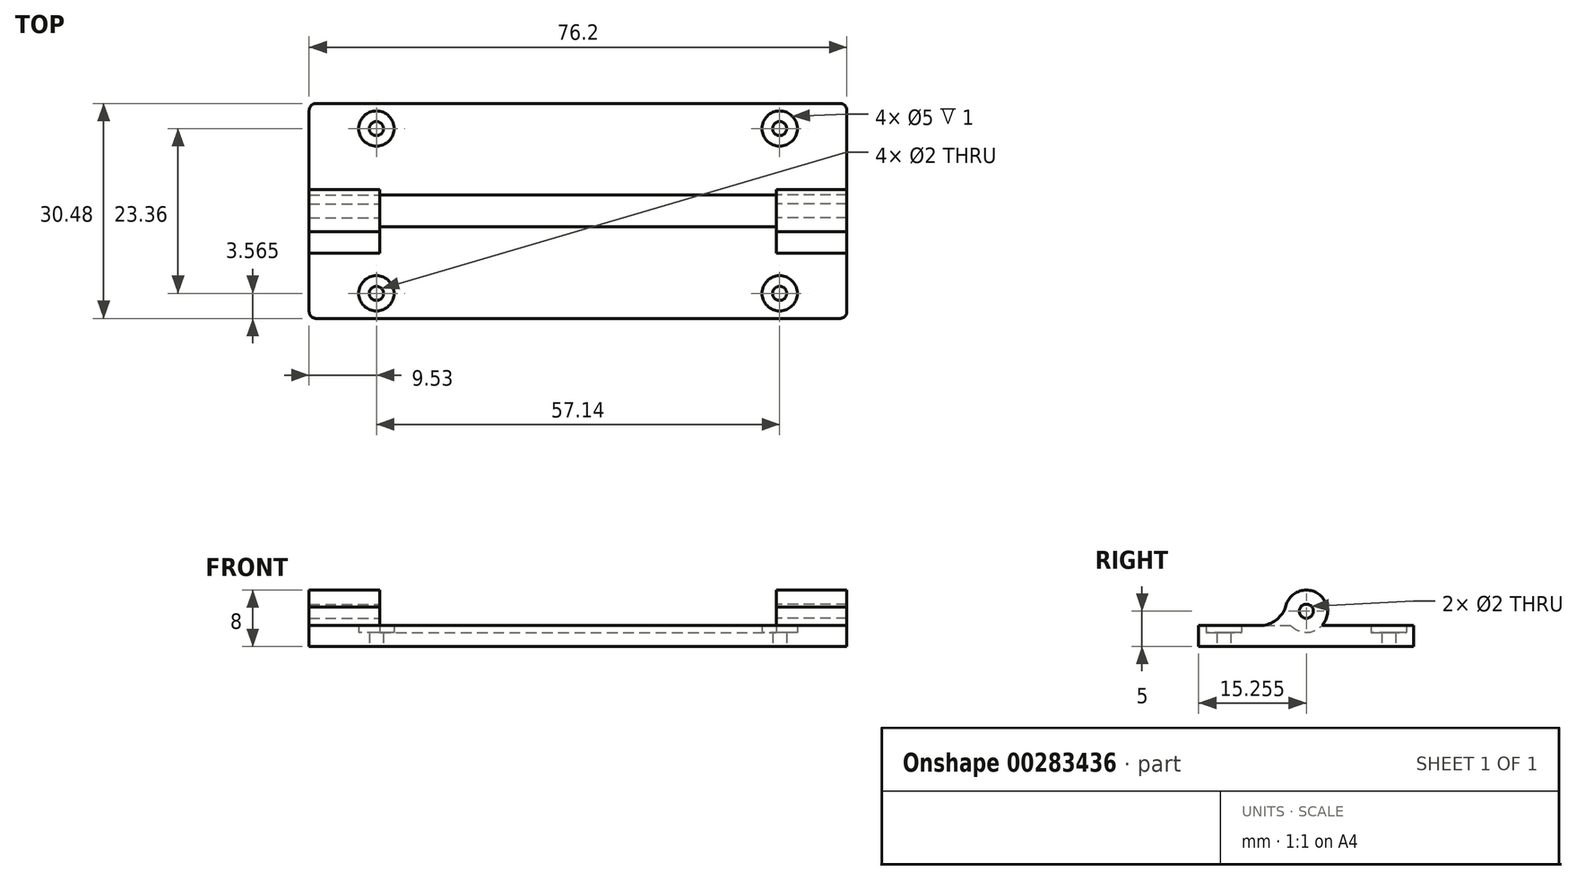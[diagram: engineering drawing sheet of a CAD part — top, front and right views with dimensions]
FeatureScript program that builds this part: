
annotation { "Feature Type Name" : "Feature", "Feature Type Description" : "" }
export const myFeature = defineFeature(function(context is Context, id is Id, definition is map)
    precondition{}
    {
        {
            var Q0;
            Q0=qCreatedBy(makeId("Top.planeOp"),FACE);
            var sketch = newSketch(context, id + "F0", { "sketchPlane" : qUnion([Q0])});
            skLineSegment(sketch, "E0.bottom", {"start": v(-38.1, -13.62) * mm, "end": v(38.1, -13.62) * mm});
            skLineSegment(sketch, "E0.top", {"start": v(-38.1, 16.86) * mm, "end": v(38.1, 16.86) * mm});
            skLineSegment(sketch, "E0.left", {"start": v(-38.1, -13.62) * mm, "end": v(-38.1, 16.86) * mm});
            skLineSegment(sketch, "E0.right", {"start": v(38.1, -13.62) * mm, "end": v(38.1, 16.86) * mm});
            skCircle(sketch, "E1", {"center": v(-28.57, -10.06) * mm, "radius": 1 * mm});
            skCircle(sketch, "E2", {"center": v(28.57, -10.06) * mm, "radius": 1 * mm});
            skCircle(sketch, "E3", {"center": v(28.57, 13.3) * mm, "radius": 1 * mm});
            skCircle(sketch, "E4", {"center": v(-28.57, 13.3) * mm, "radius": 1 * mm});
            skCircle(sketch, "E5", {"center": v(-28.57, 13.3) * mm, "radius": 2.5 * mm});
            skCircle(sketch, "E6", {"center": v(28.57, 13.3) * mm, "radius": 2.5 * mm});
            skCircle(sketch, "E7", {"center": v(28.57, -10.06) * mm, "radius": 2.5 * mm});
            skCircle(sketch, "E8", {"center": v(-28.57, -10.06) * mm, "radius": 2.5 * mm});
            skSolve(sketch);
        }
        {
            var Q0;
            Q0=qCreatedBy(makeId("Right.planeOp"),FACE);
            var sketch = newSketch(context, id + "F1", { "sketchPlane" : qUnion([Q0])});
            skLineSegment(sketch, "E9.bottom", {"start": v(-13.62, 0) * mm, "end": v(16.86, 0) * mm});
            skLineSegment(sketch, "E9.top", {"start": v(-13.62, 3) * mm, "end": v(16.86, 3) * mm});
            skLineSegment(sketch, "E9.left", {"start": v(-13.62, 0) * mm, "end": v(-13.62, 3) * mm});
            skLineSegment(sketch, "E9.right", {"start": v(16.86, 0) * mm, "end": v(16.86, 3) * mm});
            skCircle(sketch, "E10", {"center": v(1.63, 5) * mm, "radius": 3 * mm});
            skLineSegment(sketch, "E11", {"start": v(-4.37, 3) * mm, "end": v(-4.37, 5) * mm});
            skArc(sketch, "E12", {"start": v(-4.37, 3) * mm, "mid": v(-2.5, 3.87) * mm, "end": v(-1.31, 5.56) * mm});
            skLineSegment(sketch, "E13", {"start": v(1.63, 5) * mm, "end": v(1.63, 4) * mm});
            skArc(sketch, "E14.MirrorCS", {"start": v(7.63, 3) * mm, "mid": v(5.77, 3.87) * mm, "end": v(4.58, 5.56) * mm});
            skCircle(sketch, "E15", {"center": v(1.63, 5) * mm, "radius": 1 * mm});
            skSolve(sketch);
        }
        {
            var Q0;
            Q0=makeQuery(id+"F0.imprint","IMPRINT",FACE,{"disambiguationData":[TD([[makeQuery(id+"F0.imprint","IMPRINT",EDGE,{"derivedFrom":sQuery(id+"F0.wireOp",EDGE,"E0.bottom")}),1.0]])]});
            extrude(context, id + "F2", {"entities" : qUnion([Q0]), "depth" : 3 * mm, "offsetDistance" : 25 * mm});
        }
        {
            var Q0;
            Q0=makeQuery(id+"F0.imprint","IMPRINT",FACE,{"disambiguationData":[TD([[makeQuery(id+"F0.imprint","IMPRINT",EDGE,{"derivedFrom":sQuery(id+"F0.wireOp",EDGE,"E3")}),-1.0]])]});
            var Q1;
            Q1=makeQuery(id+"F0.imprint","IMPRINT",FACE,{"disambiguationData":[TD([[makeQuery(id+"F0.imprint","IMPRINT",EDGE,{"derivedFrom":sQuery(id+"F0.wireOp",EDGE,"E2")}),-1.0]])]});
            var Q2;
            Q2=makeQuery(id+"F0.imprint","IMPRINT",FACE,{"disambiguationData":[TD([[makeQuery(id+"F0.imprint","IMPRINT",EDGE,{"derivedFrom":sQuery(id+"F0.wireOp",EDGE,"E1")}),-1.0]])]});
            var Q3;
            Q3=makeQuery(id+"F0.imprint","IMPRINT",FACE,{"disambiguationData":[TD([[makeQuery(id+"F0.imprint","IMPRINT",EDGE,{"derivedFrom":sQuery(id+"F0.wireOp",EDGE,"E4")}),-1.0]])]});
            extrude(context, id + "F3", {"entities" : qUnion([Q0, Q1, Q2, Q3]), "operationType" : NewBodyOperationType.ADD, "depth" : 2 * mm, "offsetDistance" : 25 * mm});
        }
        {
            var Q0;
            {var subQ0=sQuery(id+"F1.wireOp",EDGE,"E14.MirrorCS");Q0=makeQuery(id+"F1.imprint","IMPRINT",FACE,{"disambiguationData":[TD([[makeQuery(id+"F1.imprint","IMPRINT",EDGE,{"derivedFrom":subQ0}),1.0]])]});}
            var Q1;
            {var subQ7=sQuery(id+"F1.wireOp",EDGE,"E15");var subQ8=makeQuery(id+"F1.imprint","IMPRINT",VERTEX,{"disambiguationData":[OD(0.0)],"derivedFrom":subQ7});Q1=makeQuery(id+"F1.imprint","IMPRINT",FACE,{"disambiguationData":[TD([[makeQuery(id+"F1.imprint","IMPRINT",EDGE,{"disambiguationData":[TD([[subQ8,-1.0]])],"derivedFrom":subQ7}),-1.0]])]});}
            var Q2;
            {var subQ3=sQuery(id+"F1.wireOp",EDGE,"E12");Q2=makeQuery(id+"F1.imprint","IMPRINT",FACE,{"disambiguationData":[TD([[makeQuery(id+"F1.imprint","IMPRINT",EDGE,{"derivedFrom":subQ3}),-1.0]])]});}
            extrude(context, id + "F4", {"entities" : qUnion([Q0, Q1, Q2]), "operationType" : NewBodyOperationType.ADD, "depth" : 38.1 * mm, "offsetDistance" : 25 * mm, "hasSecondDirection" : true, "secondDirectionOppositeDirection" : false, "secondDirectionDepth" : 28.1 * mm});
        }
        {
            var Q0;
            {var subQ0=sQuery(id+"F1.wireOp",EDGE,"E14.MirrorCS");Q0=makeQuery(id+"F1.imprint","IMPRINT",FACE,{"disambiguationData":[TD([[makeQuery(id+"F1.imprint","IMPRINT",EDGE,{"derivedFrom":subQ0}),1.0]])]});}
            var Q1;
            {var subQ7=sQuery(id+"F1.wireOp",EDGE,"E15");var subQ8=makeQuery(id+"F1.imprint","IMPRINT",VERTEX,{"disambiguationData":[OD(0.0)],"derivedFrom":subQ7});Q1=makeQuery(id+"F1.imprint","IMPRINT",FACE,{"disambiguationData":[TD([[makeQuery(id+"F1.imprint","IMPRINT",EDGE,{"disambiguationData":[TD([[subQ8,-1.0]])],"derivedFrom":subQ7}),-1.0]])]});}
            var Q2;
            {var subQ3=sQuery(id+"F1.wireOp",EDGE,"E12");Q2=makeQuery(id+"F1.imprint","IMPRINT",FACE,{"disambiguationData":[TD([[makeQuery(id+"F1.imprint","IMPRINT",EDGE,{"derivedFrom":subQ3}),-1.0]])]});}
            extrude(context, id + "F5", {"entities" : qUnion([Q0, Q1, Q2]), "operationType" : NewBodyOperationType.ADD, "oppositeDirection" : true, "depth" : 38.1 * mm, "offsetDistance" : 25 * mm, "hasSecondDirection" : true, "secondDirectionOppositeDirection" : true, "secondDirectionDepth" : 28.1 * mm});
        }
        {
            var Q0;
            {var subQ0=sQuery(id+"F1.wireOp",EDGE,"E10");var subQ1=sQuery(id+"F1.wireOp",EDGE,"E9.top");var subQ2=makeQuery(id+"F1.imprint","INTERSECT",VERTEX,{"disambiguationData":[OD(0.0)],"derivedFrom":[subQ1,subQ0]});Q0=makeQuery(id+"F1.imprint","IMPRINT",FACE,{"disambiguationData":[TD([[makeQuery(id+"F1.imprint","IMPRINT",EDGE,{"disambiguationData":[TD([[subQ2,-1.0]])],"derivedFrom":subQ1}),-1.0]])]});}
            extrude(context, id + "F6", {"entities" : qUnion([Q0]), "operationType" : NewBodyOperationType.REMOVE, "oppositeDirection" : true, "depth" : 28.1 * mm, "offsetDistance" : 25 * mm, "hasSecondDirection" : true, "secondDirectionOppositeDirection" : false, "secondDirectionDepth" : 28.1 * mm});
        }
        {
            var Q0;
            Q0=makeQuery(id+"F2.opExtrude","SWEPT_EDGE",EDGE,{"disambiguationData":[OSD([sQuery(id+"F0.wireOp",EDGE,"E0.bottom"),sQuery(id+"F0.wireOp",EDGE,"E0.right")])]});
            var Q1;
            Q1=makeQuery(id+"F2.opExtrude","SWEPT_EDGE",EDGE,{"disambiguationData":[OSD([sQuery(id+"F0.wireOp",EDGE,"E0.top"),sQuery(id+"F0.wireOp",EDGE,"E0.right")])]});
            var Q2;
            Q2=makeQuery(id+"F2.opExtrude","SWEPT_EDGE",EDGE,{"disambiguationData":[OSD([sQuery(id+"F0.wireOp",EDGE,"E0.top"),sQuery(id+"F0.wireOp",EDGE,"E0.left")])]});
            var Q3;
            Q3=makeQuery(id+"F2.opExtrude","SWEPT_EDGE",EDGE,{"disambiguationData":[OSD([sQuery(id+"F0.wireOp",EDGE,"E0.bottom"),sQuery(id+"F0.wireOp",EDGE,"E0.left")])]});
            fillet(context, id + "F7", {"entities" : qUnion([Q0, Q1, Q2, Q3]), "tangentPropagation" : true, "radius" : 1 * mm, "defaultsChanged" : false, "vertexSettings" : [], "allowEdgeOverflow" : false});
        }
    });
